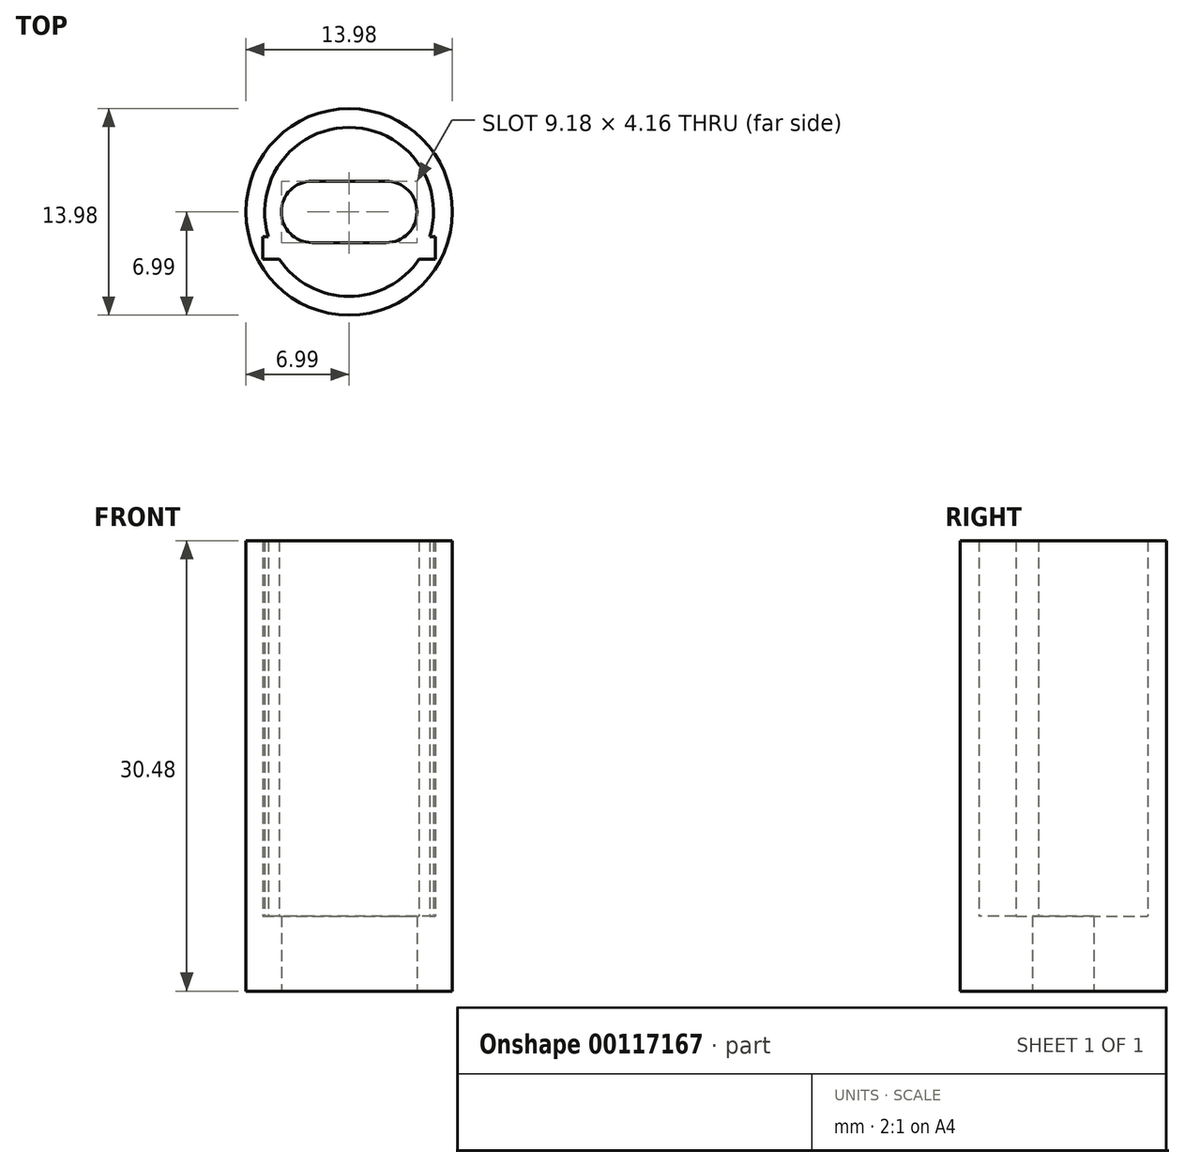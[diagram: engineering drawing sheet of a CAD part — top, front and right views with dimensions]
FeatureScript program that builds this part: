
annotation { "Feature Type Name" : "Feature", "Feature Type Description" : "" }
export const myFeature = defineFeature(function(context is Context, id is Id, definition is map)
    precondition{}
    {
        {
            var Q0;
            Q0=qCreatedBy(makeId("Top.planeOp"),FACE);
            var sketch = newSketch(context, id + "F0", { "sketchPlane" : qUnion([Q0])});
            skCircle(sketch, "E0", {"center": v(0, 0) * mm, "radius": 6.99 * mm});
            skLineSegment(sketch, "E1", {"start": v(-2.5, 2.08) * mm, "end": v(2.5, 2.08) * mm});
            skLineSegment(sketch, "E2", {"start": v(-2.5, -2.08) * mm, "end": v(2.5, -2.08) * mm});
            skArc(sketch, "E3", {"start": v(-2.5, 2.08) * mm, "mid": v(-4.6, 0) * mm, "end": v(-2.5, -2.08) * mm});
            skArc(sketch, "E4", {"start": v(2.5, -2.08) * mm, "mid": v(4.6, 0) * mm, "end": v(2.5, 2.08) * mm});
            skPoint(sketch, "E5", {"position": v(0, 2.08) * mm});
            skPoint(sketch, "E6", {"position": v(-4.6, 0) * mm});
            skPoint(sketch, "E7", {"position": v(4.6, 0) * mm});
            skSolve(sketch);
        }
        {
            var Q0;
            Q0 = qSketchRegion(id + "F0", true);
            extrude(context, id + "F1", {"entities" : qUnion([Q0]), "depth" : 5.08 * mm});
        }
        {
            var Q0;
            Q0=makeQuery(id+"F1.opExtrude","CAP_FACE",FACE,{"disambiguationData":[OSD([sQuery(id+"F0.wireOp",EDGE,"E0"),sQuery(id+"F0.wireOp",EDGE,"E1"),sQuery(id+"F0.wireOp",EDGE,"E2"),sQuery(id+"F0.wireOp",EDGE,"E3"),sQuery(id+"F0.wireOp",EDGE,"E4")])],"isStart":false});
            var sketch = newSketch(context, id + "F2", { "sketchPlane" : qUnion([Q0])});
            skCircle(sketch, "E8", {"center": v(0, 0) * mm, "radius": 6.99 * mm});
            skPoint(sketch, "E9", {"position": v(5.72, 0) * mm});
            skPoint(sketch, "E10", {"position": v(6.99, 0) * mm});
            skArc(sketch, "E11", {"start": v(-5.46, -1.68) * mm, "mid": v(-5.16, -2.47) * mm, "end": v(-4.73, -3.2) * mm, "construction": true});
            skArc(sketch, "E12", {"start": v(5.46, -1.68) * mm, "mid": v(0, 5.72) * mm, "end": v(-5.46, -1.68) * mm});
            skLineSegment(sketch, "E13", {"start": v(-5.84, -3.2) * mm, "end": v(-4.73, -3.2) * mm});
            skLineSegment(sketch, "E14", {"start": v(5.84, -3.2) * mm, "end": v(4.73, -3.2) * mm});
            skArc(sketch, "E15", {"start": v(4.73, -3.2) * mm, "mid": v(5.16, -2.47) * mm, "end": v(5.46, -1.68) * mm, "construction": true});
            skArc(sketch, "E16", {"start": v(-4.73, -3.2) * mm, "mid": v(0, -5.72) * mm, "end": v(4.73, -3.2) * mm});
            skLineSegment(sketch, "E17", {"start": v(-5.84, -3.2) * mm, "end": v(-5.84, -1.68) * mm});
            skLineSegment(sketch, "E18", {"start": v(-5.46, -1.68) * mm, "end": v(-5.84, -1.68) * mm});
            skLineSegment(sketch, "E19", {"start": v(5.46, -1.68) * mm, "end": v(5.84, -1.68) * mm});
            skLineSegment(sketch, "E20", {"start": v(5.84, -1.68) * mm, "end": v(5.84, -3.2) * mm});
            skSolve(sketch);
        }
        {
            var Q0;
            Q0 = qSketchRegion(id + "F2", true);
            extrude(context, id + "F3", {"entities" : qUnion([Q0]), "operationType" : NewBodyOperationType.ADD, "depth" : 25.4 * mm});
        }
    });
